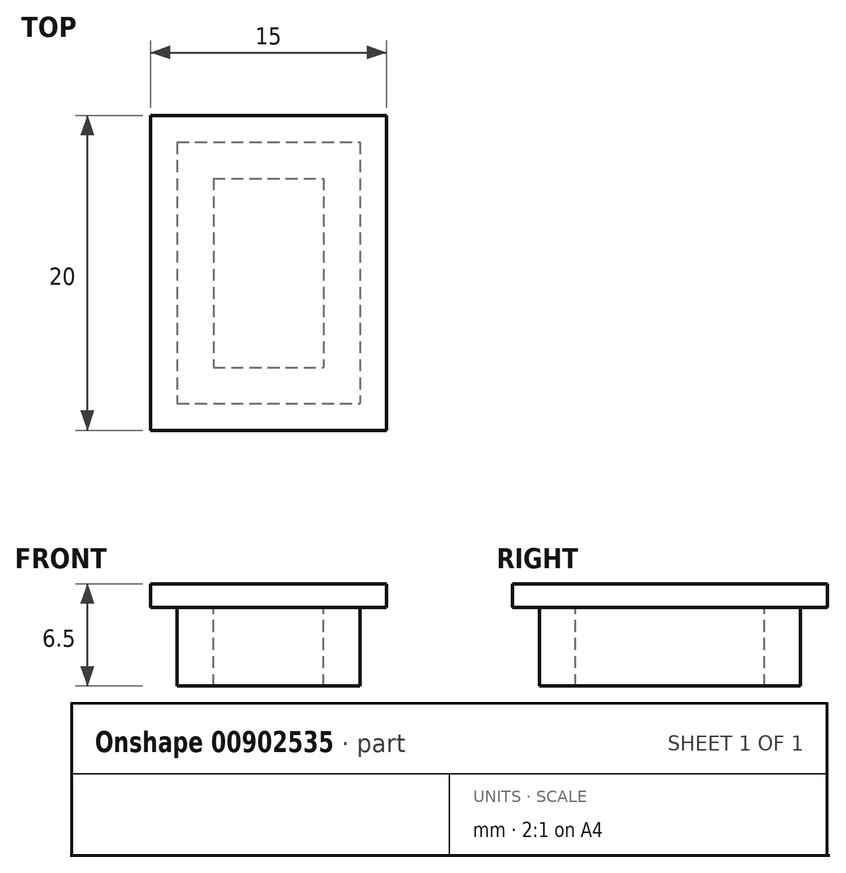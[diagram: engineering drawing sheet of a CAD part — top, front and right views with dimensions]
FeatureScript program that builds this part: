
annotation { "Feature Type Name" : "Feature", "Feature Type Description" : "" }
export const myFeature = defineFeature(function(context is Context, id is Id, definition is map)
    precondition{}
    {
        {
            var Q0;
            Q0=qCreatedBy(makeId("Top.planeOp"),FACE);
            var sketch = newSketch(context, id + "F0", { "sketchPlane" : qUnion([Q0])});
            skLineSegment(sketch, "E0.bottom", {"start": v(-3.5, 6) * mm, "end": v(3.5, 6) * mm});
            skLineSegment(sketch, "E0.top", {"start": v(-3.5, -6) * mm, "end": v(3.5, -6) * mm});
            skLineSegment(sketch, "E0.left", {"start": v(-3.5, 6) * mm, "end": v(-3.5, -6) * mm});
            skLineSegment(sketch, "E0.right", {"start": v(3.5, 6) * mm, "end": v(3.5, -6) * mm});
            skPoint(sketch, "E0.middle", {"position": v(0, 0) * mm});
            skLineSegment(sketch, "E1.bottom", {"start": v(-5.8, 8.3) * mm, "end": v(5.8, 8.3) * mm});
            skLineSegment(sketch, "E1.top", {"start": v(-5.8, -8.3) * mm, "end": v(5.8, -8.3) * mm});
            skLineSegment(sketch, "E1.left", {"start": v(-5.8, 8.3) * mm, "end": v(-5.8, -8.3) * mm});
            skLineSegment(sketch, "E1.right", {"start": v(5.8, 8.3) * mm, "end": v(5.8, -8.3) * mm});
            skLineSegment(sketch, "E2.bottom", {"start": v(-7.5, 10) * mm, "end": v(7.5, 10) * mm});
            skLineSegment(sketch, "E2.top", {"start": v(-7.5, -10) * mm, "end": v(7.5, -10) * mm});
            skLineSegment(sketch, "E2.left", {"start": v(-7.5, 10) * mm, "end": v(-7.5, -10) * mm});
            skLineSegment(sketch, "E2.right", {"start": v(7.5, 10) * mm, "end": v(7.5, -10) * mm});
            skSolve(sketch);
        }
        {
            var Q0;
            Q0 = qSketchRegion(id + "F0", true);
            var Q1;
            Q1=makeQuery(id+"F0.imprint","IMPRINT",FACE,{"disambiguationData":[TD([[makeQuery(id+"F0.imprint","IMPRINT",EDGE,{"derivedFrom":sQuery(id+"F0.wireOp",EDGE,"E0.bottom")}),1.0]])]});
            var Q2;
            Q2=makeQuery(id+"F0.imprint","IMPRINT",FACE,{"disambiguationData":[TD([[makeQuery(id+"F0.imprint","IMPRINT",EDGE,{"derivedFrom":sQuery(id+"F0.wireOp",EDGE,"E0.bottom")}),-1.0]])]});
            extrude(context, id + "F1", {"entities" : qUnion([Q0, Q1, Q2]), "depth" : 1.5 * mm, "offsetDistance" : 25 * mm});
        }
        {
            var Q0;
            Q0=makeQuery(id+"F0.imprint","IMPRINT",FACE,{"disambiguationData":[TD([[makeQuery(id+"F0.imprint","IMPRINT",EDGE,{"derivedFrom":sQuery(id+"F0.wireOp",EDGE,"E0.bottom")}),1.0]])]});
            extrude(context, id + "F2", {"entities" : qUnion([Q0]), "operationType" : NewBodyOperationType.ADD, "oppositeDirection" : true, "depth" : 5 * mm, "offsetDistance" : 25 * mm});
        }
    });
